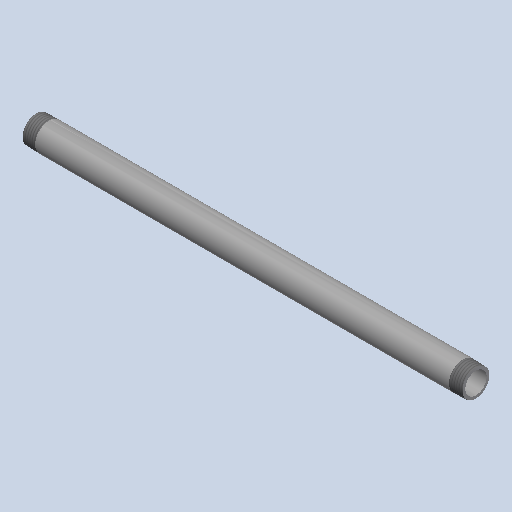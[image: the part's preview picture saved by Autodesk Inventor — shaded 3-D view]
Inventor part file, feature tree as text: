
AUTODESK INVENTOR PART (.ipt)
format: ipt  version: 2025 (Build 290162000, 162)  size: 176,128 bytes
history: native  units: mm (DEFAULTED — no unit token found)
features: other x8, revolve x1
ambient origin geometry x8: Origin, YZ Plane, XZ Plane, XY Plane, X Axis, Y Axis, Z Axis, Center Point
bodies: Solid1 (feature_tree)
feature tree (9):
  revolve  "Revolution1"  [1 undecoded]
  other  "Work Axis1"
  other  "Work Point5"
  other  "Work Axis2"
  other  "Work Point6"
  other  "Work Axis3"
  other  "Work Axis4"
  other  "Work Point7"
  other  "Work Point8"
note: 1 required parameter value undecoded (feature->parameter linkage not recoverable at this tier; creation-order binding heuristic only, values carry confidence <= 0.55)
